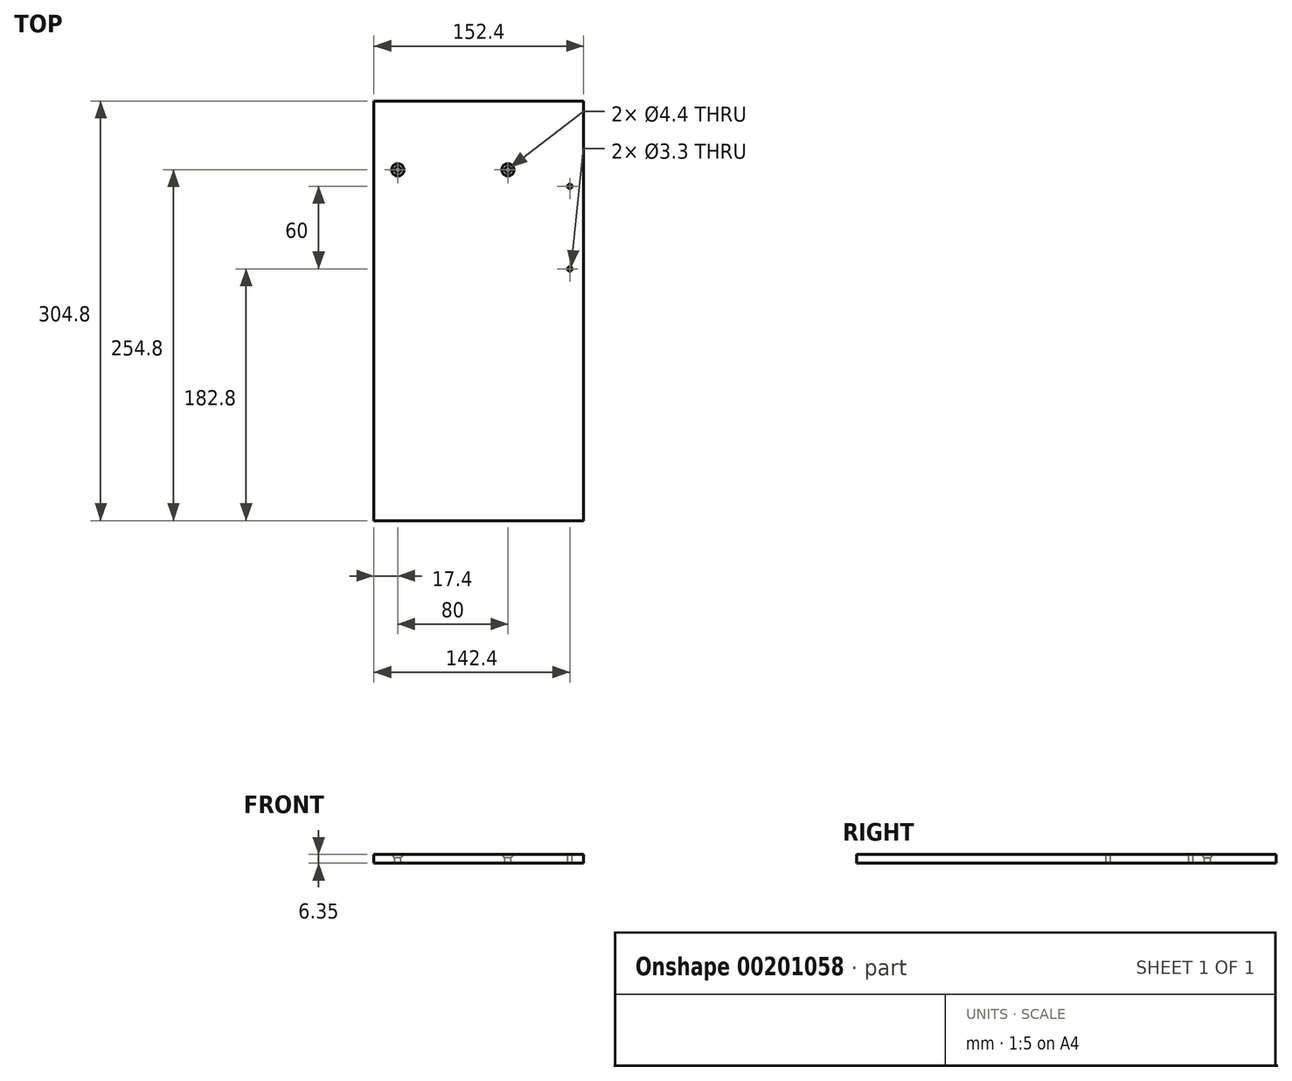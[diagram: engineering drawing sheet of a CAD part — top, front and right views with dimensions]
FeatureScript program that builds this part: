
annotation { "Feature Type Name" : "Feature", "Feature Type Description" : "" }
export const myFeature = defineFeature(function(context is Context, id is Id, definition is map)
    precondition{}
    {
        {
            var Q0;
            Q0=qCreatedBy(makeId("Top.planeOp"),FACE);
            var sketch = newSketch(context, id + "F0", { "sketchPlane" : qUnion([Q0])});
            skLineSegment(sketch, "E0.bottom", {"start": v(0, 0) * mm, "end": v(152.4, 0) * mm});
            skLineSegment(sketch, "E0.top", {"start": v(0, 304.8) * mm, "end": v(152.4, 304.8) * mm});
            skLineSegment(sketch, "E0.left", {"start": v(0, 0) * mm, "end": v(0, 304.8) * mm});
            skLineSegment(sketch, "E0.right", {"start": v(152.4, 0) * mm, "end": v(152.4, 304.8) * mm});
            skSolve(sketch);
        }
        {
            var Q0;
            Q0 = qSketchRegion(id + "F0", true);
            extrude(context, id + "F1", {"entities" : qUnion([Q0]), "oppositeDirection" : true, "depth" : 6.35 * mm});
        }
        {
            var Q0;
            Q0=makeQuery(id+"F1.opExtrude","CAP_FACE",FACE,{"disambiguationData":[OSD([sQuery(id+"F0.wireOp",EDGE,"E0.bottom"),sQuery(id+"F0.wireOp",EDGE,"E0.top"),sQuery(id+"F0.wireOp",EDGE,"E0.left"),sQuery(id+"F0.wireOp",EDGE,"E0.right")])],"isStart":true});
            var sketch = newSketch(context, id + "F2", { "sketchPlane" : qUnion([Q0])});
            skPoint(sketch, "E1", {"position": v(17.4, 254.8) * mm});
            skPoint(sketch, "E2", {"position": v(97.4, 254.8) * mm});
            skSolve(sketch);
        }
        {
            var Q0;
            Q0=sQuery(id+"F2.wireOp",VERTEX,"E2");
            var Q1;
            Q1=sQuery(id+"F2.wireOp",VERTEX,"E1");
            var Q2;
            Q2=makeQuery(id+"F1.opExtrude","SWEPT_BODY",BODY,{"disambiguationData":[OSD([sQuery(id+"F0.wireOp",EDGE,"E0.bottom"),sQuery(id+"F0.wireOp",EDGE,"E0.top"),sQuery(id+"F0.wireOp",EDGE,"E0.left"),sQuery(id+"F0.wireOp",EDGE,"E0.right")])]});
            hole(context, id + "F3", {"style" : HoleStyle.C_SINK, "endStyle" : HoleEndStyle.THROUGH, "standardTappedOrClearance" : lookupTablePath({ "standard" : "ISO", "fit" : "Normal", "size" : "M4", "type" : "Clearance" }), "standardBlindInLast" : lookupTablePath({ "fit" : "Standard", "standard" : "ISO", "size" : "M4", "type" : "Clearance" }), "holeDiameter" : 4.4 * mm, "cSinkDiameter" : 8.96 * mm, "cSinkAngle" : 90 * degree, "locations" : qUnion([Q0, Q1]), "scope" : qUnion([Q2]), "isTappedThrough" : true});
        }
        {
            var Q0;
            Q0=makeQuery(id+"F1.opExtrude","CAP_FACE",FACE,{"disambiguationData":[OSD([sQuery(id+"F0.wireOp",EDGE,"E0.bottom"),sQuery(id+"F0.wireOp",EDGE,"E0.top"),sQuery(id+"F0.wireOp",EDGE,"E0.left"),sQuery(id+"F0.wireOp",EDGE,"E0.right")])],"isStart":true});
            var sketch = newSketch(context, id + "F4", { "sketchPlane" : qUnion([Q0])});
            skPoint(sketch, "E3", {"position": v(142.4, 242.8) * mm});
            skPoint(sketch, "E4", {"position": v(142.4, 182.8) * mm});
            skSolve(sketch);
        }
        {
            var Q0;
            Q0=sQuery(id+"F4.wireOp",VERTEX,"E3");
            var Q1;
            Q1=sQuery(id+"F4.wireOp",VERTEX,"E4");
            var Q2;
            Q2=makeQuery(id+"F1.opExtrude","SWEPT_BODY",BODY,{"disambiguationData":[OSD([sQuery(id+"F0.wireOp",EDGE,"E0.bottom"),sQuery(id+"F0.wireOp",EDGE,"E0.top"),sQuery(id+"F0.wireOp",EDGE,"E0.left"),sQuery(id+"F0.wireOp",EDGE,"E0.right")])]});
            hole(context, id + "F5", {"style" : HoleStyle.SIMPLE, "endStyle" : HoleEndStyle.THROUGH, "standardTappedOrClearance" : lookupTablePath({ "standard" : "ISO", "engagement" : "75%", "pitch" : "0.7 mm", "size" : "M4", "type" : "Tapped" }), "standardBlindInLast" : lookupTablePath({ "standard" : "ISO", "engagement" : "75%", "pitch" : "0.7 mm", "size" : "M4", "type" : "Tapped" }), "holeDiameter" : 3.3 * mm, "locations" : qUnion([Q0, Q1]), "scope" : qUnion([Q2]), "isTappedThrough" : true, "majorDiameter" : 4 * mm, "showTappedDepth" : true});
        }
    });
